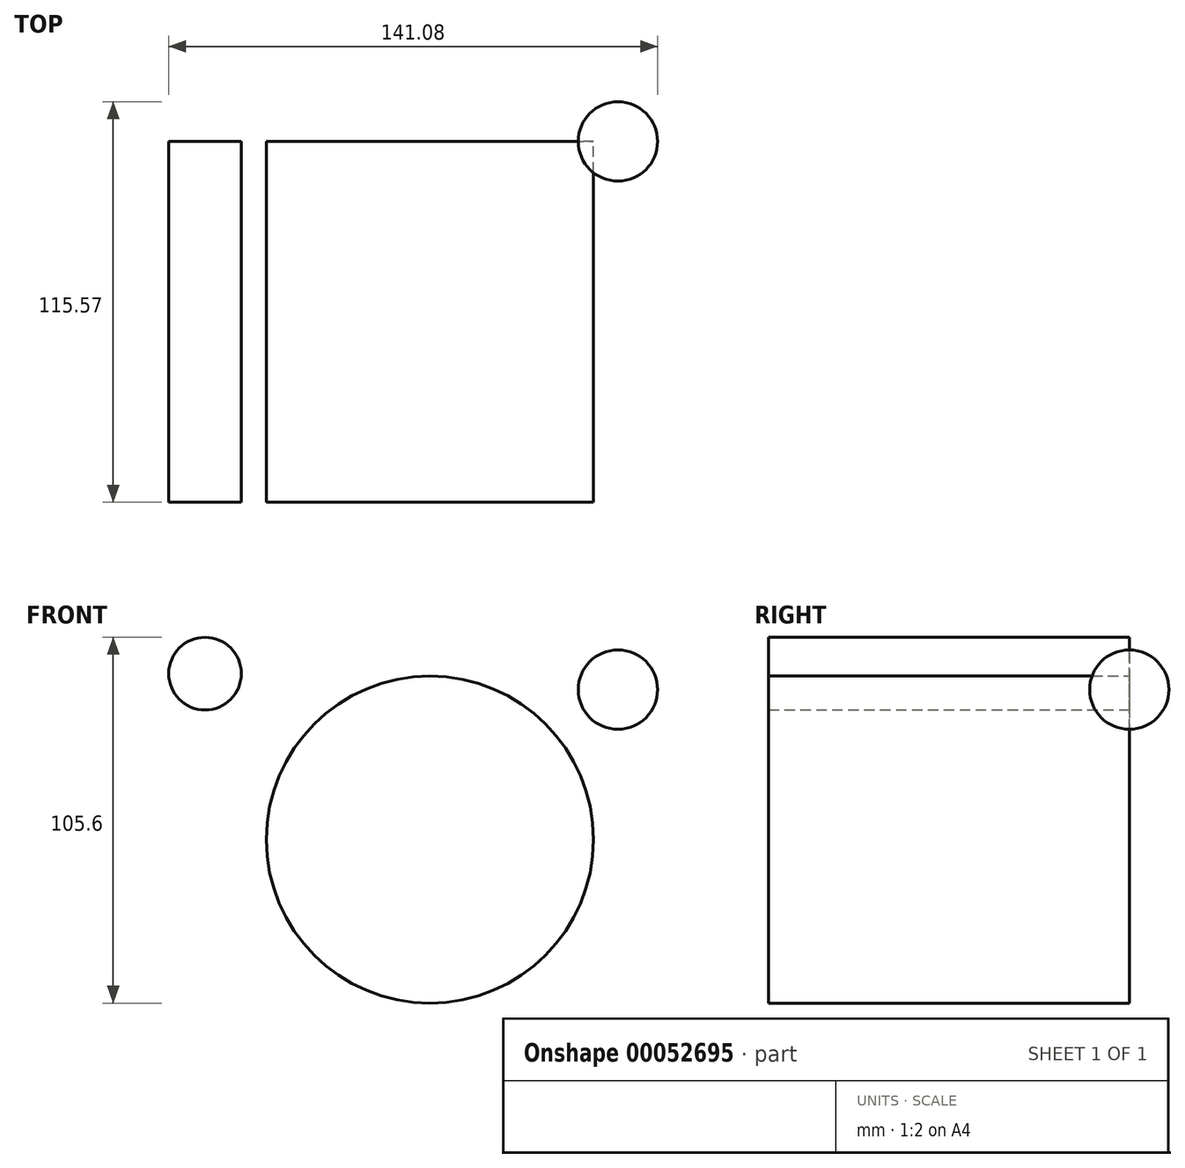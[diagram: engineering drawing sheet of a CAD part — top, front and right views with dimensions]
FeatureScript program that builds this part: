
annotation { "Feature Type Name" : "Feature", "Feature Type Description" : "" }
export const myFeature = defineFeature(function(context is Context, id is Id, definition is map)
    precondition{}
    {
        {
            var Q0;
            Q0=qCreatedBy(makeId("Front.planeOp"),FACE);
            var sketch = newSketch(context, id + "F0", { "sketchPlane" : qUnion([Q0])});
            skCircle(sketch, "E0", {"center": v(0, 0) * mm, "radius": 45.01 * mm});
            skCircle(sketch, "E1", {"center": v(-76.66, 52.76) * mm, "radius": 14.09 * mm});
            skCircle(sketch, "E2", {"center": v(54.26, 43.3) * mm, "radius": 11.45 * mm});
            skLineSegment(sketch, "E3", {"start": v(54.26, 54.74) * mm, "end": v(54.26, 31.85) * mm});
            skSolve(sketch);
        }
        {
            var Q0;
            {var subQ0=sQuery(id+"F0.wireOp",EDGE,"E3");Q0=makeQuery(id+"F0.imprint","IMPRINT",FACE,{"disambiguationData":[TD([[makeQuery(id+"F0.imprint","IMPRINT",EDGE,{"derivedFrom":subQ0}),-1.0]])]});}
            var Q1;
            Q1=sQuery(id+"F0.wireOp",EDGE,"E3");
            revolve(context, id + "F1", {"entities" : qUnion([Q0]), "axis" : qUnion([Q1]), "revolveType" : RevolveType.FULL});
        }
        {
            var Q0;
            Q0=qCreatedBy(makeId("Front.planeOp"),FACE);
            var sketch = newSketch(context, id + "F2", { "sketchPlane" : qUnion([Q0])});
            skCircle(sketch, "E4", {"center": v(0, 0) * mm, "radius": 47.2 * mm});
            skCircle(sketch, "E5", {"center": v(-64.89, 47.91) * mm, "radius": 10.48 * mm});
            skSolve(sketch);
        }
        {
            var Q0;
            Q0=makeQuery(id+"F2.imprint","IMPRINT",FACE,{"disambiguationData":[TD([[makeQuery(id+"F2.imprint","IMPRINT",EDGE,{"derivedFrom":sQuery(id+"F2.wireOp",EDGE,"E5")}),1.0]])]});
            var Q1;
            Q1=makeQuery(id+"F2.imprint","IMPRINT",FACE,{"disambiguationData":[TD([[makeQuery(id+"F2.imprint","IMPRINT",EDGE,{"derivedFrom":sQuery(id+"F2.wireOp",EDGE,"E4")}),1.0]])]});
            extrude(context, id + "F3", {"entities" : qUnion([Q0, Q1]), "depth" : 104.12 * mm});
        }
    });
